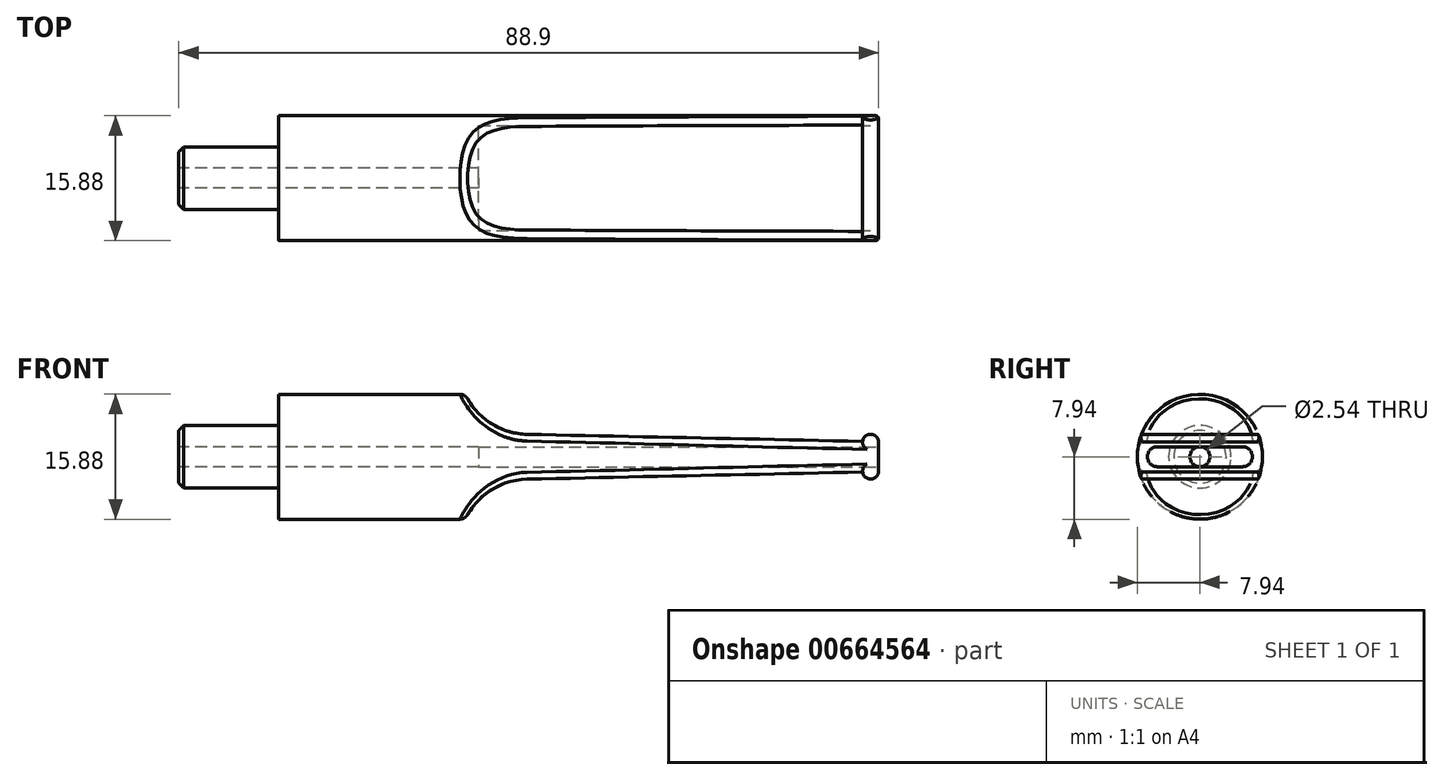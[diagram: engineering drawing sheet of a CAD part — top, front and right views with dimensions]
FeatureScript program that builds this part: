
annotation { "Feature Type Name" : "Feature", "Feature Type Description" : "" }
export const myFeature = defineFeature(function(context is Context, id is Id, definition is map)
    precondition{}
    {
        {
            var Q0;
            Q0=qCreatedBy(makeId("Right.planeOp"),FACE);
            var sketch = newSketch(context, id + "F0", { "sketchPlane" : qUnion([Q0])});
            skCircle(sketch, "E0", {"center": v(0, 0) * mm, "radius": 7.94 * mm});
            skCircle(sketch, "E1", {"center": v(0, 0) * mm, "radius": 1.27 * mm});
            skSolve(sketch);
        }
        {
            var Q0;
            Q0 = qSketchRegion(id + "F0", true);
            extrude(context, id + "F1", {"entities" : qUnion([Q0]), "depth" : 76.2 * mm, "offsetDistance" : 25.4 * mm});
        }
        {
            var Q0;
            Q0=makeQuery(id+"F1.opExtrude","CAP_FACE",FACE,{"disambiguationData":[OSD([sQuery(id+"F0.wireOp",EDGE,"E0"),sQuery(id+"F0.wireOp",EDGE,"E1")])],"isStart":true});
            var sketch = newSketch(context, id + "F2", { "sketchPlane" : qUnion([Q0])});
            skCircle(sketch, "E2", {"center": v(0, 0) * mm, "radius": 3.97 * mm});
            skCircle(sketch, "E3.0", {"center": v(0, 0) * mm, "radius": 1.27 * mm});
            skSolve(sketch);
        }
        {
            var Q0;
            Q0 = qSketchRegion(id + "F2", true);
            extrude(context, id + "F3", {"entities" : qUnion([Q0]), "operationType" : NewBodyOperationType.ADD, "depth" : 12.7 * mm, "offsetDistance" : 25.4 * mm});
        }
        {
            var Q0;
            Q0=makeQuery(id+"F3.opExtrude","CAP_EDGE",EDGE,{"disambiguationData":[OSD([sQuery(id+"F2.wireOp",EDGE,"E2")])],"isStart":false});
            chamfer(context, id + "F4", {"entities" : qUnion([Q0]), "width" : 0.64 * mm, "tangentPropagation" : true});
        }
        {
            var Q0;
            Q0=qCreatedBy(makeId("Front.planeOp"),FACE);
            var sketch = newSketch(context, id + "F5", { "sketchPlane" : qUnion([Q0])});
            skLineSegment(sketch, "E4", {"start": v(76.2, 1.9) * mm, "end": v(76.2, 1.9) * mm});
            skArc(sketch, "E5", {"start": v(23.7, 7.94) * mm, "mid": v(26.9, 4.28) * mm, "end": v(31.55, 2.85) * mm});
            skLineSegment(sketch, "E6", {"start": v(74.18, 1.95) * mm, "end": v(31.55, 2.85) * mm});
            skArc(sketch, "E7", {"start": v(76.2, 1.9) * mm, "mid": v(75.2, 2.86) * mm, "end": v(74.18, 1.95) * mm});
            skLineSegment(sketch, "E8", {"start": v(76.2, 1.9) * mm, "end": v(76.2, 7.94) * mm});
            skLineSegment(sketch, "E9", {"start": v(76.2, 7.94) * mm, "end": v(23.7, 7.94) * mm});
            skArc(sketch, "E10.MirrorCS", {"start": v(76.2, -1.9) * mm, "mid": v(75.2, -2.86) * mm, "end": v(74.18, -1.95) * mm});
            skLineSegment(sketch, "E11.MirrorCS", {"start": v(74.18, -1.95) * mm, "end": v(31.55, -2.85) * mm});
            skArc(sketch, "E12.MirrorCS", {"start": v(23.7, -7.94) * mm, "mid": v(26.9, -4.28) * mm, "end": v(31.55, -2.85) * mm});
            skLineSegment(sketch, "E13.MirrorCS", {"start": v(76.2, -7.94) * mm, "end": v(23.7, -7.94) * mm});
            skLineSegment(sketch, "E14.MirrorCS", {"start": v(76.2, -1.9) * mm, "end": v(76.2, -7.94) * mm});
            skSolve(sketch);
        }
        {
            var Q0;
            Q0 = qSketchRegion(id + "F5", true);
            extrude(context, id + "F6", {"entities" : qUnion([Q0]), "operationType" : NewBodyOperationType.REMOVE, "endBound" : BoundingType.SYMMETRIC, "oppositeDirection" : true, "depth" : 25.4 * mm, "offsetDistance" : 25.4 * mm});
        }
        {
            var Q0;
            Q0=makeQuery(id+"F6.boolean.opBoolean","INTERSECT",EDGE,{"disambiguationData":[OD(0.0)],"derivedFrom":[makeQuery(id+"F1.opExtrude","SWEPT_FACE",FACE,{"disambiguationData":[OSD([sQuery(id+"F0.wireOp",EDGE,"E0")])]}),makeQuery(id+"F6.opExtrude","SWEPT_FACE",FACE,{"disambiguationData":[OSD([sQuery(id+"F5.wireOp",EDGE,"E6")])]})]});
            var Q1;
            Q1=makeQuery(id+"F6.boolean.opBoolean","INTERSECT",EDGE,{"disambiguationData":[OD(0.0)],"derivedFrom":[makeQuery(id+"F1.opExtrude","SWEPT_FACE",FACE,{"disambiguationData":[OSD([sQuery(id+"F0.wireOp",EDGE,"E0")])]}),makeQuery(id+"F6.opExtrude","SWEPT_FACE",FACE,{"disambiguationData":[OSD([sQuery(id+"F5.wireOp",EDGE,"E11.MirrorCS")])]})]});
            fillet(context, id + "F7", {"entities" : qUnion([Q0, Q1]), "radius" : 1.14 * mm, "tangentPropagation" : true, "allowEdgeOverflow" : false});
        }
        {
            var Q0;
            Q0=makeQuery(id+"F1.opExtrude","CAP_FACE",FACE,{"disambiguationData":[OSD([sQuery(id+"F0.wireOp",EDGE,"E0"),sQuery(id+"F0.wireOp",EDGE,"E1")])],"isStart":false});
            var sketch = newSketch(context, id + "F8", { "sketchPlane" : qUnion([Q0])});
            skLineSegment(sketch, "E15.bottom", {"start": v(-5.4, 1.27) * mm, "end": v(5.4, 1.27) * mm});
            skLineSegment(sketch, "E15.top", {"start": v(-5.4, -1.27) * mm, "end": v(5.4, -1.27) * mm});
            skLineSegment(sketch, "E15.left", {"start": v(-6.67, 0) * mm, "end": v(-6.67, 0) * mm});
            skLineSegment(sketch, "E15.right", {"start": v(6.67, 0) * mm, "end": v(6.67, 0) * mm});
            skPoint(sketch, "E15.middle", {"position": v(0, 0) * mm});
            skPoint(sketch, "E16.visualSharp", {"position": v(-6.67, 1.27) * mm});
            skArc(sketch, "E16.filletArc", {"start": v(-5.4, 1.27) * mm, "mid": v(-6.3, 0.9) * mm, "end": v(-6.67, 0) * mm});
            skPoint(sketch, "E17.visualSharp", {"position": v(-6.67, -1.27) * mm});
            skArc(sketch, "E17.filletArc", {"start": v(-6.67, 0) * mm, "mid": v(-6.3, -0.9) * mm, "end": v(-5.4, -1.27) * mm});
            skPoint(sketch, "E18.visualSharp", {"position": v(6.67, -1.27) * mm});
            skArc(sketch, "E18.filletArc", {"start": v(5.4, -1.27) * mm, "mid": v(6.3, -0.9) * mm, "end": v(6.67, 0) * mm});
            skPoint(sketch, "E19.visualSharp", {"position": v(6.67, 1.27) * mm});
            skArc(sketch, "E19.filletArc", {"start": v(6.67, 0) * mm, "mid": v(6.3, 0.9) * mm, "end": v(5.4, 1.27) * mm});
            skSolve(sketch);
        }
        {
            var Q0;
            Q0 = qSketchRegion(id + "F8", true);
            extrude(context, id + "F9", {"entities" : qUnion([Q0]), "operationType" : NewBodyOperationType.REMOVE, "oppositeDirection" : true, "depth" : 50.8 * mm, "offsetDistance" : 25.4 * mm});
        }
        {
            var Q0;
            Q0=makeQuery(id+"F6.boolean.opBoolean","SPLIT",EDGE,{"disambiguationData":[OD(0.0)],"derivedFrom":makeQuery(id+"F1.opExtrude","CAP_EDGE",EDGE,{"disambiguationData":[OSD([sQuery(id+"F0.wireOp",EDGE,"E0")])],"isStart":false})});
            var Q1;
            Q1=makeQuery(id+"F6.boolean.opBoolean","SPLIT",EDGE,{"disambiguationData":[OD(1.0)],"derivedFrom":makeQuery(id+"F1.opExtrude","CAP_EDGE",EDGE,{"disambiguationData":[OSD([sQuery(id+"F0.wireOp",EDGE,"E0")])],"isStart":false})});
            fillet(context, id + "F10", {"entities" : qUnion([Q0, Q1]), "radius" : 0.38 * mm, "tangentPropagation" : true, "allowEdgeOverflow" : false});
        }
    });
